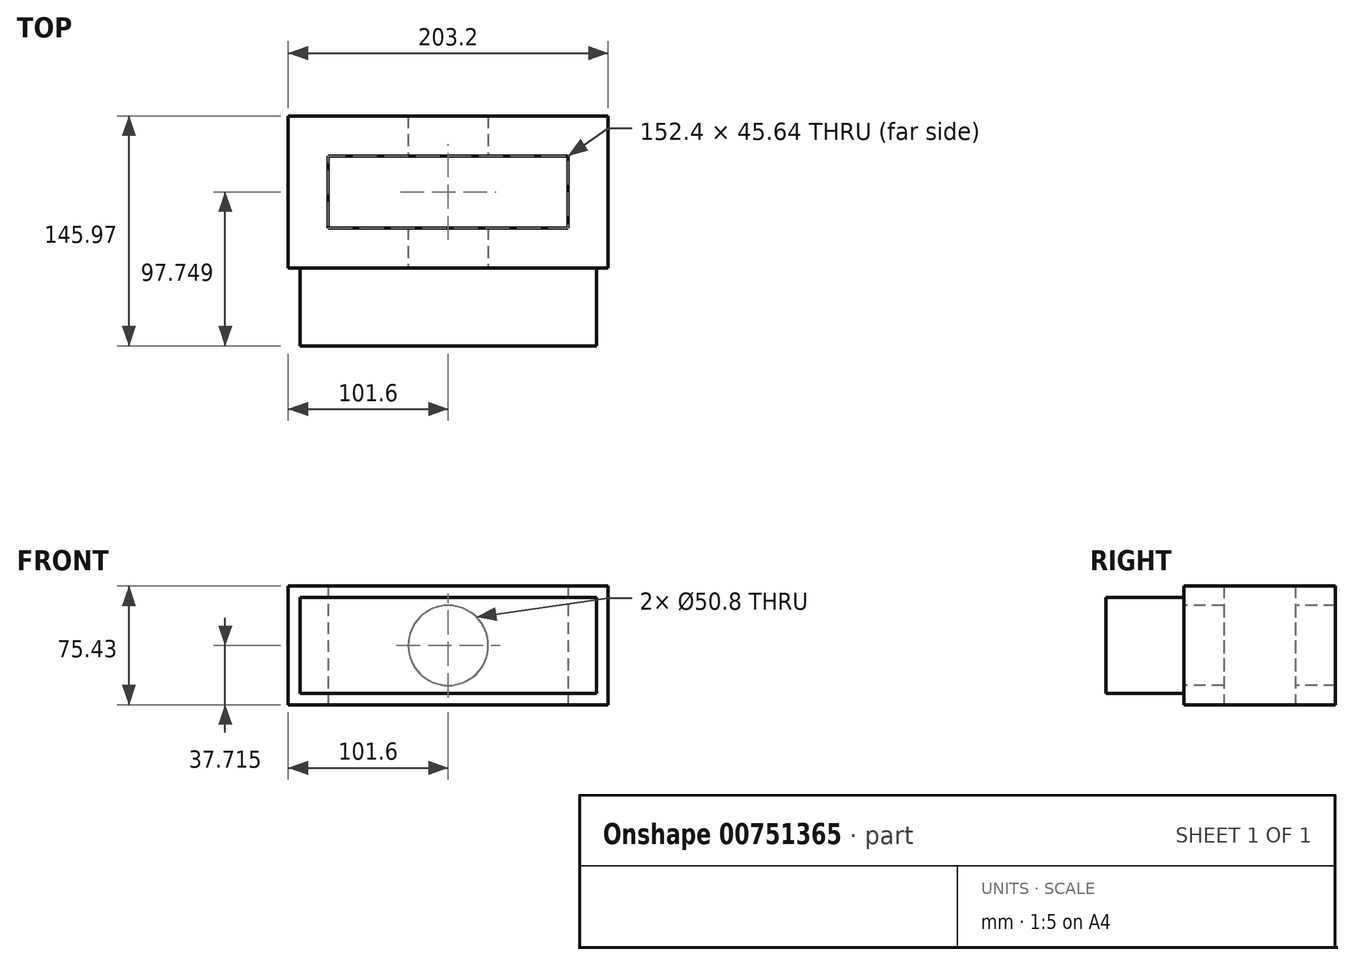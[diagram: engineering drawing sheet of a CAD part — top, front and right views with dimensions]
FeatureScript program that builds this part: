
annotation { "Feature Type Name" : "Feature", "Feature Type Description" : "" }
export const myFeature = defineFeature(function(context is Context, id is Id, definition is map)
    precondition{}
    {
        {
            var Q0;
            Q0=qCreatedBy(makeId("Top.planeOp"),FACE);
            var sketch = newSketch(context, id + "F0", { "sketchPlane" : qUnion([Q0])});
            skLineSegment(sketch, "E0.bottom", {"start": v(0, 0) * mm, "end": v(203.2, 0) * mm});
            skLineSegment(sketch, "E0.top", {"start": v(0, -96.44) * mm, "end": v(203.2, -96.44) * mm});
            skLineSegment(sketch, "E0.left", {"start": v(0, 0) * mm, "end": v(0, -96.44) * mm});
            skLineSegment(sketch, "E0.right", {"start": v(203.2, 0) * mm, "end": v(203.2, -96.44) * mm});
            skLineSegment(sketch, "E1.bottom", {"start": v(25.4, -25.4) * mm, "end": v(177.8, -25.4) * mm});
            skLineSegment(sketch, "E1.top", {"start": v(25.4, -71.04) * mm, "end": v(177.8, -71.04) * mm});
            skLineSegment(sketch, "E1.left", {"start": v(25.4, -25.4) * mm, "end": v(25.4, -71.04) * mm});
            skLineSegment(sketch, "E1.right", {"start": v(177.8, -25.4) * mm, "end": v(177.8, -71.04) * mm});
            skSolve(sketch);
        }
        {
            var Q0;
            Q0 = qSketchRegion(id + "F0", true);
            extrude(context, id + "F1", {"entities" : qUnion([Q0]), "depth" : 49.78 * mm, "offsetDistance" : 25.4 * mm, "hasSecondDirection" : true, "secondDirectionOppositeDirection" : true, "secondDirectionDepth" : 25.65 * mm});
        }
        {
            var Q0;
            Q0=makeQuery(id+"F1.opExtrude","SWEPT_FACE",FACE,{"disambiguationData":[OSD([sQuery(id+"F0.wireOp",EDGE,"E0.top")])]});
            var sketch = newSketch(context, id + "F2", { "sketchPlane" : qUnion([Q0])});
            skCircle(sketch, "E2", {"center": v(101.6, 12.07) * mm, "radius": 25.4 * mm});
            skPoint(sketch, "E2.centerSnap0", {"position": v(101.6, 49.78) * mm});
            skPoint(sketch, "E2.centerSnap1", {"position": v(0, 12.07) * mm});
            skSolve(sketch);
        }
        {
            var Q0;
            Q0 = qSketchRegion(id + "F2", true);
            var Q1;
            Q1=makeQuery(id+"F1.opExtrude","SWEPT_FACE",FACE,{"disambiguationData":[OSD([sQuery(id+"F0.wireOp",EDGE,"E0.bottom")])]});
            extrude(context, id + "F3", {"entities" : qUnion([Q0]), "operationType" : NewBodyOperationType.REMOVE, "endBound" : BoundingType.UP_TO_SURFACE, "oppositeDirection" : true, "depth" : 48.77 * mm, "endBoundEntityFace" : qUnion([Q1]), "offsetDistance" : 25.4 * mm});
        }
        {
            var Q0;
            Q0=makeQuery(id+"F1.opExtrude","SWEPT_FACE",FACE,{"disambiguationData":[OSD([sQuery(id+"F0.wireOp",EDGE,"E0.top")])]});
            var sketch = newSketch(context, id + "F4", { "sketchPlane" : qUnion([Q0])});
            skLineSegment(sketch, "E3.0", {"start": v(7.37, -18.29) * mm, "end": v(195.83, -18.29) * mm});
            skLineSegment(sketch, "E3.1", {"start": v(7.37, 42.42) * mm, "end": v(7.37, -18.29) * mm});
            skLineSegment(sketch, "E3.2", {"start": v(7.37, 42.42) * mm, "end": v(195.83, 42.42) * mm});
            skLineSegment(sketch, "E3.3", {"start": v(195.83, 42.42) * mm, "end": v(195.83, -18.29) * mm});
            skSolve(sketch);
        }
        {
            var Q0;
            Q0 = qSketchRegion(id + "F4", true);
            extrude(context, id + "F5", {"entities" : qUnion([Q0]), "depth" : 49.53 * mm, "offsetDistance" : 25.4 * mm});
        }
    });
